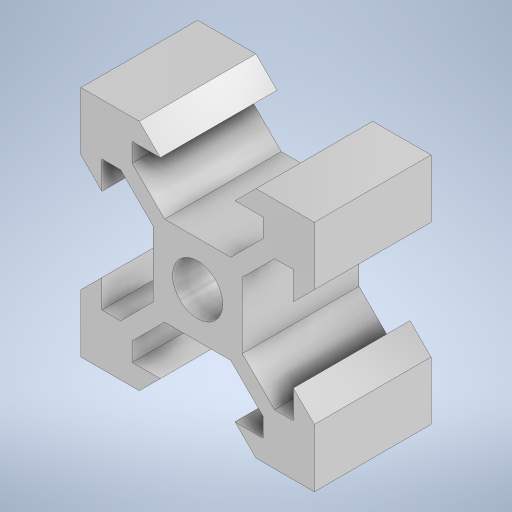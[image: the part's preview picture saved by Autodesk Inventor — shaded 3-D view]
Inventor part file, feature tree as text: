
AUTODESK INVENTOR PART (.ipt)
format: ipt  version: 2024.2 (Build 282272000, 272)  size: 311,296 bytes
history: native  units: mm
features: extrude x1, sketch x1
ambient origin geometry x8: Origin, YZ Plane, XZ Plane, XY Plane, X Axis, Y Axis, Z Axis, Center Point
bodies: Solid1 (feature_tree)
feature tree (2):
  extrude  "Extrusion1"  Depth=10.0mm
  sketch  "Sketch1"  dims[d16=10.0mm d19=3.2mm d21=4.4mm d22=4.4mm d24=45.0deg d25=1.8mm d27=1.8mm d28=45.0deg d29=3.2mm d31=1.4mm d33=2.15mm d34=3.825mm d35=3.825mm d36=135.0deg d37=40.0mm d39=360.0deg d41=10.0mm d42=0.0mm]
